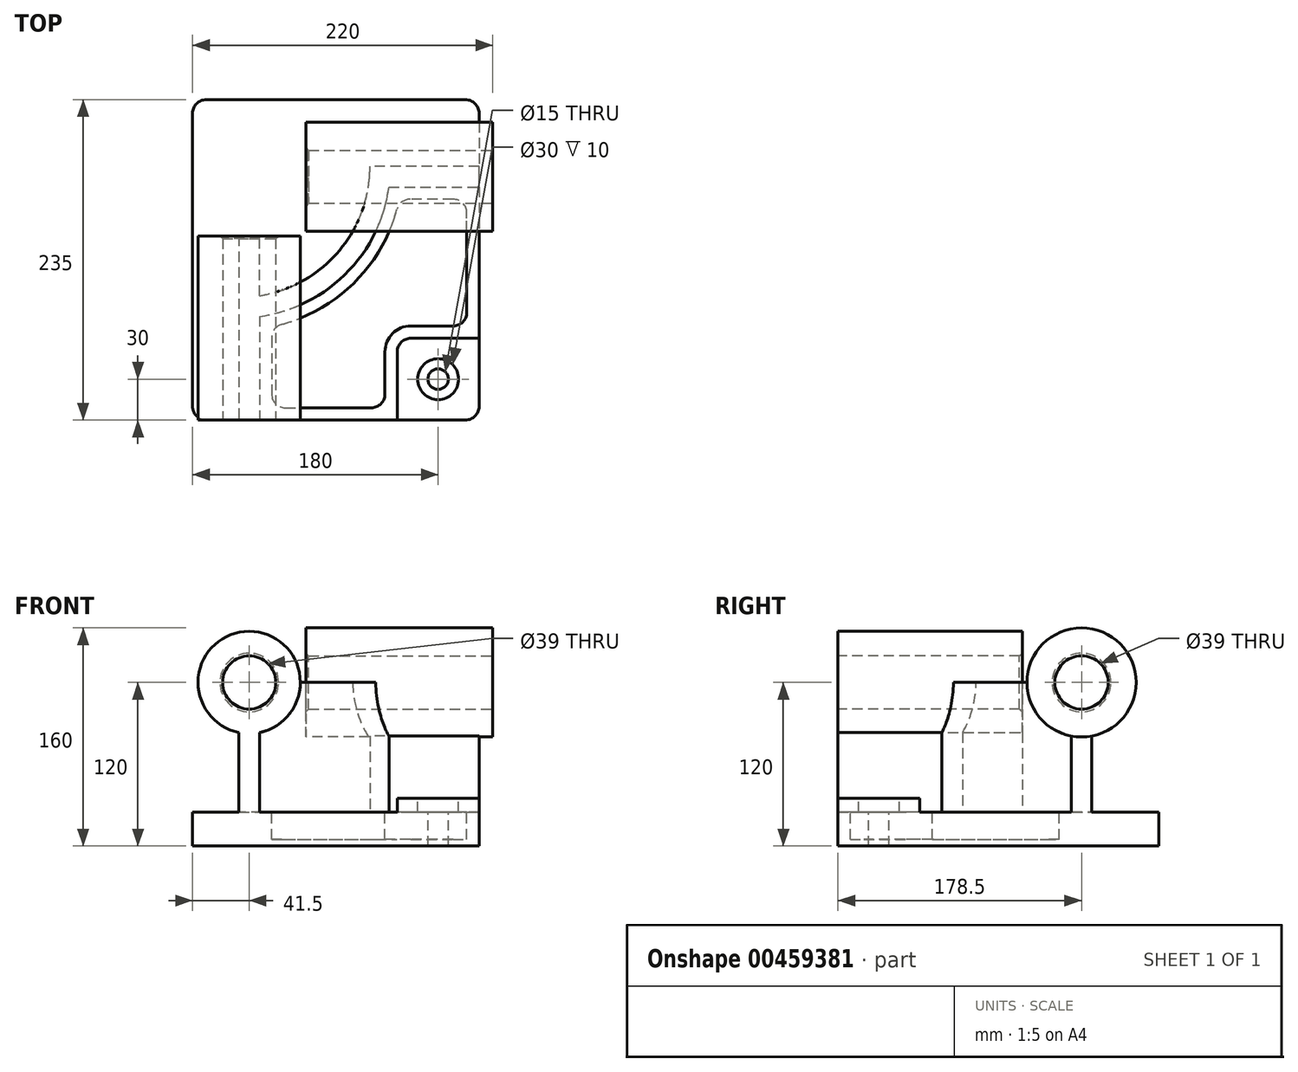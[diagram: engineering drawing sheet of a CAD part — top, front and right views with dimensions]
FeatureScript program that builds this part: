
annotation { "Feature Type Name" : "Feature", "Feature Type Description" : "" }
export const myFeature = defineFeature(function(context is Context, id is Id, definition is map)
    precondition{}
    {
        {
            var Q0;
            Q0=qCreatedBy(makeId("Top.planeOp"),FACE);
            var sketch = newSketch(context, id + "F0", { "sketchPlane" : qUnion([Q0])});
            skLineSegment(sketch, "E0.bottom", {"start": v(105, 112.5) * mm, "end": v(-105, 112.5) * mm});
            skLineSegment(sketch, "E0.top", {"start": v(105, -112.5) * mm, "end": v(-105, -112.5) * mm});
            skLineSegment(sketch, "E0.left", {"start": v(105, 112.5) * mm, "end": v(105, -112.5) * mm});
            skLineSegment(sketch, "E0.right", {"start": v(-105, 112.5) * mm, "end": v(-105, -112.5) * mm});
            skPoint(sketch, "E0.middle", {"position": v(0, 0) * mm});
            skSolve(sketch);
        }
        {
            var Q0;
            Q0 = qSketchRegion(id + "F0", true);
            extrude(context, id + "F1", {"entities" : qUnion([Q0]), "depth" : 25 * mm});
        }
        {
            var Q0;
            Q0=makeQuery(id+"F1.opExtrude","CAP_FACE",FACE,{"disambiguationData":[OSD([sQuery(id+"F0.wireOp",EDGE,"E0.bottom"),sQuery(id+"F0.wireOp",EDGE,"E0.top"),sQuery(id+"F0.wireOp",EDGE,"E0.left"),sQuery(id+"F0.wireOp",EDGE,"E0.right")])],"isStart":false});
            var sketch = newSketch(context, id + "F2", { "sketchPlane" : qUnion([Q0])});
            skLineSegment(sketch, "E1", {"start": v(-71, -32.5) * mm, "end": v(-71, -112.5) * mm});
            skLineSegment(sketch, "E2", {"start": v(25, 63.5) * mm, "end": v(105, 63.5) * mm});
            skArc(sketch, "E3", {"start": v(-71, -32.5) * mm, "mid": v(-3.12, -4.38) * mm, "end": v(25, 63.5) * mm});
            skLineSegment(sketch, "E4.0", {"start": v(-56, -46.48) * mm, "end": v(-56, -112.5) * mm});
            skArc(sketch, "E4.1", {"start": v(-56, -46.48) * mm, "mid": v(7.49, -14.99) * mm, "end": v(38.98, 48.5) * mm});
            skLineSegment(sketch, "E4.2", {"start": v(38.98, 48.5) * mm, "end": v(105, 48.5) * mm});
            skSolve(sketch);
        }
        {
            var Q0;
            Q0 = qSketchRegion(id + "F2", true);
            var Q1;
            {var subQ4=sQuery(id+"F2.wireOp",EDGE,"E1");Q1=makeQuery(id+"F2.imprint","IMPRINT",FACE,{"disambiguationData":[TD([[makeQuery(id+"F2.imprint","IMPRINT",EDGE,{"derivedFrom":subQ4}),1.0]])]});}
            extrude(context, id + "F3", {"entities" : qUnion([Q0, Q1]), "operationType" : NewBodyOperationType.ADD, "depth" : 95 * mm});
        }
        {
            var Q0;
            {var subQ0=sQuery(id+"F0.wireOp",EDGE,"E0.top");Q0=makeQuery(id+"F3.boolean.opBoolean","MERGE",FACE,{"derivedFrom":[makeQuery(id+"F1.opExtrude","SWEPT_FACE",FACE,{"disambiguationData":[OSD([subQ0])]}),makeQuery(id+"F3.opExtrude","SWEPT_FACE",FACE,{"disambiguationData":[OSD([subQ0])]})]});}
            var sketch = newSketch(context, id + "F4", { "sketchPlane" : qUnion([Q0])});
            skCircle(sketch, "E5", {"center": v(-63.5, 120) * mm, "radius": 37.5 * mm});
            skSolve(sketch);
        }
        {
            var Q0;
            Q0 = qSketchRegion(id + "F4", true);
            var Q1;
            {var subQ0=sQuery(id+"F0.wireOp",EDGE,"E0.top");Q1=makeQuery(id+"F4.imprint","IMPRINT",FACE,{"disambiguationData":[TD([[makeQuery(id+"F4.imprint","IMPRINT",EDGE,{"derivedFrom":makeQuery(id+"F1.opExtrude","CAP_EDGE",EDGE,{"disambiguationData":[OSD([subQ0])],"isStart":true})}),-1.0]])]});}
            extrude(context, id + "F5", {"entities" : qUnion([Q0, Q1]), "operationType" : NewBodyOperationType.ADD, "depth" : 10 * mm, "hasSecondDirection" : true, "secondDirectionOppositeDirection" : true, "secondDirectionDepth" : (135 - 10) * mm});
        }
        {
            var Q0;
            {var subQ0=sQuery(id+"F0.wireOp",EDGE,"E0.left");Q0=makeQuery(id+"F5.boolean.opBoolean","MERGE",FACE,{"derivedFrom":[makeQuery(id+"F3.boolean.opBoolean","MERGE",FACE,{"derivedFrom":[makeQuery(id+"F1.opExtrude","SWEPT_FACE",FACE,{"disambiguationData":[OSD([subQ0])]}),makeQuery(id+"F3.opExtrude","SWEPT_FACE",FACE,{"disambiguationData":[OSD([subQ0])]})]}),makeQuery(id+"F5.opExtrude","SWEPT_FACE",FACE,{"disambiguationData":[OSD([sQuery(id+"F0.wireOp",EDGE,"E0.top"),subQ0])]})]});}
            var sketch = newSketch(context, id + "F6", { "sketchPlane" : qUnion([Q0])});
            skCircle(sketch, "E6", {"center": v(56, 120) * mm, "radius": 40 * mm});
            skSolve(sketch);
        }
        {
            var Q0;
            Q0 = qSketchRegion(id + "F6", true);
            var Q1;
            {var subQ1=sQuery(id+"F0.wireOp",EDGE,"E0.left");var subQ6=makeQuery(id+"F3.opExtrude","CAP_EDGE",EDGE,{"disambiguationData":[OSD([subQ1])],"isStart":false});Q1=makeQuery(id+"F6.imprint","IMPRINT",FACE,{"disambiguationData":[TD([[makeQuery(id+"F6.imprint","IMPRINT",EDGE,{"derivedFrom":subQ6}),-1.0]])]});}
            extrude(context, id + "F7", {"entities" : qUnion([Q0, Q1]), "operationType" : NewBodyOperationType.ADD, "depth" : 10 * mm, "hasSecondDirection" : true, "secondDirectionOppositeDirection" : true, "secondDirectionDepth" : (137 - 10) * mm});
        }
        {
            var Q0;
            {var subQ0=sQuery(id+"F0.wireOp",EDGE,"E0.left");var subQ1=makeQuery(id+"F1.opExtrude","SWEPT_FACE",FACE,{"disambiguationData":[OSD([subQ0])]});var subQ2=makeQuery(id+"F3.opExtrude","SWEPT_FACE",FACE,{"disambiguationData":[OSD([sQuery(id+"F2.wireOp",EDGE,"E4.0")])]});var subQ3=sQuery(id+"F0.wireOp",EDGE,"E0.top");var subQ5=makeQuery(id+"F1.opExtrude","CAP_FACE",FACE,{"disambiguationData":[OSD([sQuery(id+"F0.wireOp",EDGE,"E0.bottom"),subQ3,subQ0,sQuery(id+"F0.wireOp",EDGE,"E0.right")])],"isStart":false});Q0=makeQuery(id+"F5.boolean.opBoolean","MERGE",FACE,{"derivedFrom":[makeQuery(id+"F3.boolean.opBoolean","SPLIT",FACE,{"disambiguationData":[TD([subQ2])],"derivedFrom":subQ5}),makeQuery(id+"F5.opExtrude","SWEPT_FACE",FACE,{"disambiguationData":[OSD([subQ3]),TDD([makeQuery(id+"F4.imprint","IMPRINT",EDGE,{"derivedFrom":makeQuery(id+"F3.boolean.opBoolean","SPLIT",EDGE,{"disambiguationData":[TD([subQ1])],"derivedFrom":makeQuery(id+"F1.opExtrude","CAP_EDGE",EDGE,{"disambiguationData":[OSD([subQ3])],"isStart":false})})})])]})]});}
            var sketch = newSketch(context, id + "F8", { "sketchPlane" : qUnion([Q0])});
            skLineSegment(sketch, "E7.bottom", {"start": v(105, -122.5) * mm, "end": v(45, -122.5) * mm});
            skLineSegment(sketch, "E7.top", {"start": v(105, -62.5) * mm, "end": v(45, -62.5) * mm});
            skLineSegment(sketch, "E7.left", {"start": v(105, -122.5) * mm, "end": v(105, -62.5) * mm});
            skLineSegment(sketch, "E7.right", {"start": v(45, -122.5) * mm, "end": v(45, -62.5) * mm});
            skSolve(sketch);
        }
        {
            var Q0;
            Q0 = qSketchRegion(id + "F8", true);
            var Q1;
            Q1=makeQuery(id+"F8.imprint","IMPRINT",FACE,{"disambiguationData":[TD([[makeQuery(id+"F8.imprint","IMPRINT",EDGE,{"derivedFrom":sQuery(id+"F8.wireOp",EDGE,"E7.bottom")}),-1.0]])]});
            extrude(context, id + "F9", {"entities" : qUnion([Q0, Q1]), "operationType" : NewBodyOperationType.ADD, "depth" : 10 * mm});
        }
        {
            var Q0;
            Q0=makeQuery(id+"F9.opExtrude","SWEPT_EDGE",EDGE,{"disambiguationData":[OSD([sQuery(id+"F8.wireOp",EDGE,"E7.top"),sQuery(id+"F8.wireOp",EDGE,"E7.right")])]});
            fillet(context, id + "F10", {"entities" : qUnion([Q0]), "radius" : 10 * mm, "tangentPropagation" : true, "allowEdgeOverflow" : false});
        }
        {
            var Q0;
            {var subQ0=sQuery(id+"F0.wireOp",EDGE,"E0.left");var subQ1=makeQuery(id+"F1.opExtrude","SWEPT_FACE",FACE,{"disambiguationData":[OSD([subQ0])]});var subQ2=makeQuery(id+"F3.opExtrude","SWEPT_FACE",FACE,{"disambiguationData":[OSD([sQuery(id+"F2.wireOp",EDGE,"E4.0")])]});var subQ3=sQuery(id+"F0.wireOp",EDGE,"E0.top");var subQ5=makeQuery(id+"F1.opExtrude","CAP_FACE",FACE,{"disambiguationData":[OSD([sQuery(id+"F0.wireOp",EDGE,"E0.bottom"),subQ3,subQ0,sQuery(id+"F0.wireOp",EDGE,"E0.right")])],"isStart":false});Q0=makeQuery(id+"F5.boolean.opBoolean","MERGE",FACE,{"derivedFrom":[makeQuery(id+"F3.boolean.opBoolean","SPLIT",FACE,{"disambiguationData":[TD([subQ2])],"derivedFrom":subQ5}),makeQuery(id+"F5.opExtrude","SWEPT_FACE",FACE,{"disambiguationData":[OSD([subQ3]),TDD([makeQuery(id+"F4.imprint","IMPRINT",EDGE,{"derivedFrom":makeQuery(id+"F3.boolean.opBoolean","SPLIT",EDGE,{"disambiguationData":[TD([subQ1])],"derivedFrom":makeQuery(id+"F1.opExtrude","CAP_EDGE",EDGE,{"disambiguationData":[OSD([subQ3])],"isStart":false})})})])]})]});}
            var sketch = newSketch(context, id + "F11", { "sketchPlane" : qUnion([Q0])});
            skLineSegment(sketch, "E8.0", {"start": v(-47, -54.08) * mm, "end": v(-47, -113.5) * mm});
            skArc(sketch, "E8.1", {"start": v(46.58, 39.5) * mm, "mid": v(13.85, -21.35) * mm, "end": v(-47, -54.08) * mm});
            skLineSegment(sketch, "E8.2", {"start": v(-47, -113.5) * mm, "end": v(36, -113.5) * mm});
            skLineSegment(sketch, "E8.3", {"start": v(96, 39.5) * mm, "end": v(46.58, 39.5) * mm});
            skLineSegment(sketch, "E8.4", {"start": v(36, -113.5) * mm, "end": v(36, -72.5) * mm});
            skArc(sketch, "E8.5", {"start": v(36, -72.5) * mm, "mid": v(41.56, -59.06) * mm, "end": v(55, -53.5) * mm});
            skLineSegment(sketch, "E8.6", {"start": v(55, -53.5) * mm, "end": v(96, -53.5) * mm});
            skLineSegment(sketch, "E8.7", {"start": v(96, -53.5) * mm, "end": v(96, 39.5) * mm});
            skSolve(sketch);
        }
        {
            var Q0;
            Q0=makeQuery(id+"F11.imprint","IMPRINT",FACE,{"disambiguationData":[TD([[makeQuery(id+"F11.imprint","IMPRINT",EDGE,{"derivedFrom":sQuery(id+"F11.wireOp",EDGE,"E8.0")}),1.0]])]});
            extrude(context, id + "F12", {"entities" : qUnion([Q0]), "operationType" : NewBodyOperationType.REMOVE, "oppositeDirection" : true, "depth" : 20 * mm});
        }
        {
            var Q0;
            Q0=makeQuery(id+"F9.opExtrude","CAP_FACE",FACE,{"disambiguationData":[OSD([sQuery(id+"F8.wireOp",EDGE,"E7.bottom"),sQuery(id+"F8.wireOp",EDGE,"E7.top"),sQuery(id+"F8.wireOp",EDGE,"E7.left"),sQuery(id+"F8.wireOp",EDGE,"E7.right")])],"isStart":false});
            var sketch = newSketch(context, id + "F13", { "sketchPlane" : qUnion([Q0])});
            skCircle(sketch, "E9", {"center": v(75, -92.5) * mm, "radius": 15 * mm});
            skSolve(sketch);
        }
        {
            var Q0;
            Q0=sQuery(id+"F13.wireOp",VERTEX,"E9.center");
            var Q1;
            Q1=makeQuery(id+"F1.opExtrude","SWEPT_BODY",BODY,{"disambiguationData":[OSD([sQuery(id+"F0.wireOp",EDGE,"E0.bottom"),sQuery(id+"F0.wireOp",EDGE,"E0.top"),sQuery(id+"F0.wireOp",EDGE,"E0.left"),sQuery(id+"F0.wireOp",EDGE,"E0.right")])]});
            hole(context, id + "F14", {"style" : HoleStyle.C_BORE, "endStyle" : HoleEndStyle.THROUGH, "holeDiameter" : 15 * mm, "cBoreDiameter" : 30 * mm, "cBoreDepth" : 10 * mm, "isTappedThrough" : true, "tappedDepth" : 12 * mm, "tapClearance" : 3, "startFromSketch" : true, "locations" : qUnion([Q0]), "scope" : qUnion([Q1])});
        }
        {
            var Q0;
            Q0=makeQuery(id+"F12.boolean.opBoolean","COPY",EDGE,{"derivedFrom":makeQuery(id+"F12.opExtrude","SWEPT_EDGE",EDGE,{"disambiguationData":[OSD([sQuery(id+"F11.wireOp",EDGE,"E8.0"),sQuery(id+"F11.wireOp",EDGE,"E8.1")])]})});
            var Q1;
            Q1=makeQuery(id+"F12.boolean.opBoolean","COPY",EDGE,{"derivedFrom":makeQuery(id+"F12.opExtrude","SWEPT_EDGE",EDGE,{"disambiguationData":[OSD([sQuery(id+"F11.wireOp",EDGE,"E8.1"),sQuery(id+"F11.wireOp",EDGE,"E8.3")])]})});
            var Q2;
            Q2=makeQuery(id+"F12.boolean.opBoolean","COPY",EDGE,{"derivedFrom":makeQuery(id+"F12.opExtrude","SWEPT_EDGE",EDGE,{"disambiguationData":[OSD([sQuery(id+"F11.wireOp",EDGE,"E8.0"),sQuery(id+"F11.wireOp",EDGE,"E8.2")])]})});
            var Q3;
            Q3=makeQuery(id+"F12.boolean.opBoolean","COPY",EDGE,{"derivedFrom":makeQuery(id+"F12.opExtrude","SWEPT_EDGE",EDGE,{"disambiguationData":[OSD([sQuery(id+"F11.wireOp",EDGE,"E8.3"),sQuery(id+"F11.wireOp",EDGE,"E8.7")])]})});
            var Q4;
            Q4=makeQuery(id+"F12.boolean.opBoolean","COPY",EDGE,{"derivedFrom":makeQuery(id+"F12.opExtrude","SWEPT_EDGE",EDGE,{"disambiguationData":[OSD([sQuery(id+"F11.wireOp",EDGE,"E8.6"),sQuery(id+"F11.wireOp",EDGE,"E8.7")])]})});
            var Q5;
            Q5=makeQuery(id+"F12.boolean.opBoolean","COPY",EDGE,{"derivedFrom":makeQuery(id+"F12.opExtrude","SWEPT_EDGE",EDGE,{"disambiguationData":[OSD([sQuery(id+"F11.wireOp",EDGE,"E8.2"),sQuery(id+"F11.wireOp",EDGE,"E8.4")])]})});
            fillet(context, id + "F15", {"entities" : qUnion([Q0, Q1, Q2, Q3, Q4, Q5]), "radius" : 10 * mm, "tangentPropagation" : true, "allowEdgeOverflow" : false});
        }
        {
            var Q0;
            Q0=makeQuery(id+"F9.boolean.opBoolean","MERGE",FACE,{"derivedFrom":[makeQuery(id+"F5.opExtrude","CAP_FACE",FACE,{"disambiguationData":[OSD([sQuery(id+"F0.wireOp",EDGE,"E0.top"),sQuery(id+"F0.wireOp",EDGE,"E0.left"),sQuery(id+"F0.wireOp",EDGE,"E0.right"),sQuery(id+"F2.wireOp",EDGE,"E1"),sQuery(id+"F2.wireOp",EDGE,"E4.0"),sQuery(id+"F4.wireOp",EDGE,"E5")])],"isStart":false}),makeQuery(id+"F9.opExtrude","SWEPT_FACE",FACE,{"disambiguationData":[OSD([sQuery(id+"F8.wireOp",EDGE,"E7.bottom")])]})]});
            var sketch = newSketch(context, id + "F16", { "sketchPlane" : qUnion([Q0])});
            skCircle(sketch, "E10", {"center": v(-63.5, 120) * mm, "radius": 19.5 * mm});
            skSolve(sketch);
        }
        {
            var Q0;
            Q0 = qSketchRegion(id + "F16", true);
            extrude(context, id + "F17", {"entities" : qUnion([Q0]), "operationType" : NewBodyOperationType.REMOVE, "endBound" : BoundingType.THROUGH_ALL, "oppositeDirection" : true, "depth" : 25 * mm});
        }
        {
            var Q0;
            Q0=makeQuery(id+"F7.opExtrude","CAP_FACE",FACE,{"disambiguationData":[OSD([sQuery(id+"F6.wireOp",EDGE,"E6")])],"isStart":false});
            var sketch = newSketch(context, id + "F18", { "sketchPlane" : qUnion([Q0])});
            skCircle(sketch, "E11", {"center": v(56, 120) * mm, "radius": 19.5 * mm});
            skSolve(sketch);
        }
        {
            var Q0;
            Q0 = qSketchRegion(id + "F18", true);
            extrude(context, id + "F19", {"entities" : qUnion([Q0]), "operationType" : NewBodyOperationType.REMOVE, "endBound" : BoundingType.THROUGH_ALL, "oppositeDirection" : true, "depth" : 25 * mm});
        }
        {
            var Q0;
            Q0=makeQuery(id+"F19.boolean.opBoolean","COPY",EDGE,{"derivedFrom":makeQuery(id+"F19.opExtrude","CAP_EDGE",EDGE,{"disambiguationData":[OSD([sQuery(id+"F18.wireOp",EDGE,"E11")])],"isStart":true})});
            var Q1;
            Q1=makeQuery(id+"F17.boolean.opBoolean","COPY",EDGE,{"derivedFrom":makeQuery(id+"F17.opExtrude","CAP_EDGE",EDGE,{"disambiguationData":[OSD([sQuery(id+"F16.wireOp",EDGE,"E10")])],"isStart":true})});
            var Q2;
            Q2=makeQuery(id+"F19.boolean.opBoolean","INTERSECT",EDGE,{"derivedFrom":[makeQuery(id+"F7.opExtrude","CAP_FACE",FACE,{"disambiguationData":[OSD([sQuery(id+"F6.wireOp",EDGE,"E6")])],"isStart":true}),makeQuery(id+"F19.opExtrude","SWEPT_FACE",FACE,{"disambiguationData":[OSD([sQuery(id+"F18.wireOp",EDGE,"E11")])]})]});
            var Q3;
            Q3=makeQuery(id+"F17.boolean.opBoolean","INTERSECT",EDGE,{"derivedFrom":[makeQuery(id+"F5.opExtrude","CAP_FACE",FACE,{"disambiguationData":[OSD([sQuery(id+"F0.wireOp",EDGE,"E0.top"),sQuery(id+"F0.wireOp",EDGE,"E0.left"),sQuery(id+"F0.wireOp",EDGE,"E0.right"),sQuery(id+"F2.wireOp",EDGE,"E1"),sQuery(id+"F2.wireOp",EDGE,"E4.0"),sQuery(id+"F4.wireOp",EDGE,"E5")])],"isStart":true}),makeQuery(id+"F17.opExtrude","SWEPT_FACE",FACE,{"disambiguationData":[OSD([sQuery(id+"F16.wireOp",EDGE,"E10")])]})]});
            chamfer(context, id + "F20", {"entities" : qUnion([Q0, Q1, Q2, Q3]), "width" : 2 * mm, "tangentPropagation" : true});
        }
        {
            var Q0;
            Q0=makeQuery(id+"F1.opExtrude","SWEPT_EDGE",EDGE,{"disambiguationData":[OSD([sQuery(id+"F0.wireOp",EDGE,"E0.bottom"),sQuery(id+"F0.wireOp",EDGE,"E0.left")])]});
            var Q1;
            Q1=makeQuery(id+"F9.boolean.opBoolean","MERGE",EDGE,{"derivedFrom":[makeQuery(id+"F5.opExtrude","CAP_EDGE",EDGE,{"disambiguationData":[OSD([sQuery(id+"F0.wireOp",EDGE,"E0.top"),sQuery(id+"F0.wireOp",EDGE,"E0.left")])],"isStart":false}),makeQuery(id+"F9.opExtrude","SWEPT_EDGE",EDGE,{"disambiguationData":[OSD([sQuery(id+"F8.wireOp",EDGE,"E7.bottom"),sQuery(id+"F8.wireOp",EDGE,"E7.left")])]})]});
            var Q2;
            Q2=makeQuery(id+"F5.opExtrude","CAP_EDGE",EDGE,{"disambiguationData":[OSD([sQuery(id+"F0.wireOp",EDGE,"E0.top"),sQuery(id+"F0.wireOp",EDGE,"E0.right")])],"isStart":false});
            var Q3;
            Q3=makeQuery(id+"F1.opExtrude","SWEPT_EDGE",EDGE,{"disambiguationData":[OSD([sQuery(id+"F0.wireOp",EDGE,"E0.bottom"),sQuery(id+"F0.wireOp",EDGE,"E0.right")])]});
            fillet(context, id + "F21", {"entities" : qUnion([Q0, Q1, Q2, Q3]), "radius" : 10 * mm, "tangentPropagation" : true, "allowEdgeOverflow" : false});
        }
    });
